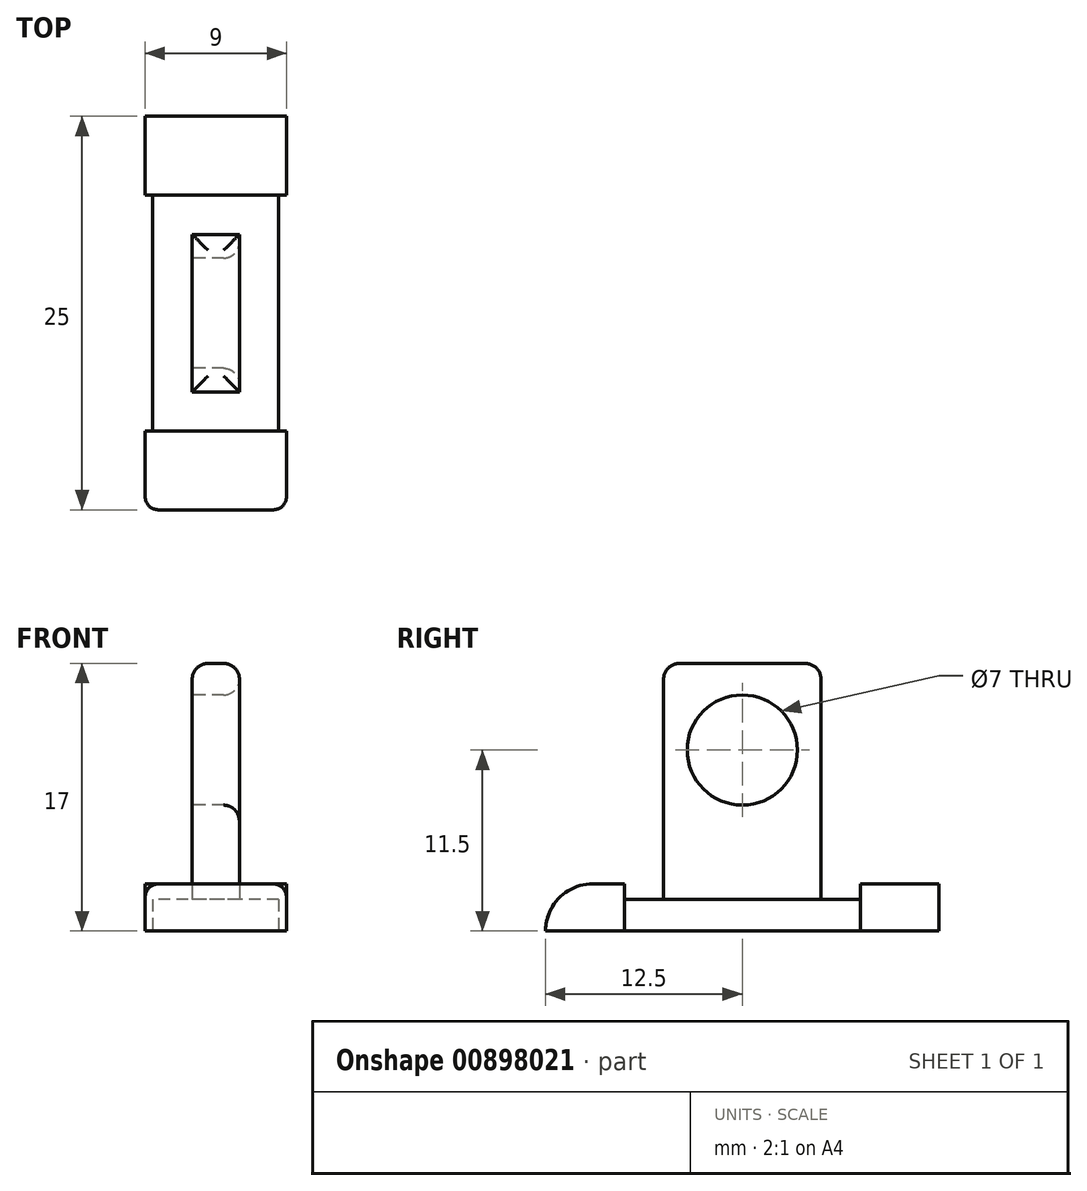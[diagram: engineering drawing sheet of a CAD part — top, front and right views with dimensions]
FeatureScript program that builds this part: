
annotation { "Feature Type Name" : "Feature", "Feature Type Description" : "" }
export const myFeature = defineFeature(function(context is Context, id is Id, definition is map)
    precondition{}
    {
        {
            var Q0;
            Q0=qCreatedBy(makeId("Top.planeOp"),FACE);
            var sketch = newSketch(context, id + "F0", { "sketchPlane" : qUnion([Q0])});
            skLineSegment(sketch, "E0.bottom", {"start": v(4, -10) * mm, "end": v(-4, -10) * mm});
            skLineSegment(sketch, "E0.top", {"start": v(4, 10) * mm, "end": v(-4, 10) * mm});
            skLineSegment(sketch, "E0.left", {"start": v(4, -10) * mm, "end": v(4, 10) * mm});
            skLineSegment(sketch, "E0.right", {"start": v(-4, -10) * mm, "end": v(-4, 10) * mm});
            skPoint(sketch, "E0.middle", {"position": v(0, 0) * mm});
            skLineSegment(sketch, "E1.bottom", {"start": v(4.5, 7.5) * mm, "end": v(-4.5, 7.5) * mm});
            skLineSegment(sketch, "E1.top", {"start": v(4.5, 12.5) * mm, "end": v(-4.5, 12.5) * mm});
            skLineSegment(sketch, "E1.left", {"start": v(4.5, 7.5) * mm, "end": v(4.5, 12.5) * mm});
            skLineSegment(sketch, "E1.right", {"start": v(-4.5, 7.5) * mm, "end": v(-4.5, 12.5) * mm});
            skPoint(sketch, "E1.middle", {"position": v(0, 10) * mm});
            skLineSegment(sketch, "E2.bottom", {"start": v(4.5, -12.5) * mm, "end": v(-4.5, -12.5) * mm});
            skLineSegment(sketch, "E2.top", {"start": v(4.5, -7.5) * mm, "end": v(-4.5, -7.5) * mm});
            skLineSegment(sketch, "E2.left", {"start": v(4.5, -12.5) * mm, "end": v(4.5, -7.5) * mm});
            skLineSegment(sketch, "E2.right", {"start": v(-4.5, -12.5) * mm, "end": v(-4.5, -7.5) * mm});
            skPoint(sketch, "E2.middle", {"position": v(0, -10) * mm});
            skSolve(sketch);
        }
        {
            var Q0;
            {var subQ0=sQuery(id+"F0.wireOp",EDGE,"E2.top");var subQ1=sQuery(id+"F0.wireOp",EDGE,"E0.left");var subQ2=makeQuery(id+"F0.imprint","INTERSECT",VERTEX,{"derivedFrom":[subQ1,subQ0]});Q0=makeQuery(id+"F0.imprint","IMPRINT",FACE,{"disambiguationData":[TD([[makeQuery(id+"F0.imprint","IMPRINT",EDGE,{"disambiguationData":[TD([[subQ2,-1.0]])],"derivedFrom":subQ1}),1.0]])]});}
            extrude(context, id + "F1", {"entities" : qUnion([Q0]), "depth" : 2 * mm, "offsetDistance" : 25 * mm});
        }
        {
            var Q0;
            {var subQ0=sQuery(id+"F0.wireOp",EDGE,"E0.bottom");Q0=makeQuery(id+"F0.imprint","IMPRINT",FACE,{"disambiguationData":[TD([[makeQuery(id+"F0.imprint","IMPRINT",EDGE,{"derivedFrom":subQ0}),-1.0]])]});}
            var Q1;
            {var subQ1=sQuery(id+"F0.wireOp",EDGE,"E0.bottom");Q1=makeQuery(id+"F0.imprint","IMPRINT",FACE,{"disambiguationData":[TD([[makeQuery(id+"F0.imprint","IMPRINT",EDGE,{"derivedFrom":subQ1}),1.0]])]});}
            var Q2;
            {var subQ5=sQuery(id+"F0.wireOp",EDGE,"E0.top");Q2=makeQuery(id+"F0.imprint","IMPRINT",FACE,{"disambiguationData":[TD([[makeQuery(id+"F0.imprint","IMPRINT",EDGE,{"derivedFrom":subQ5}),-1.0]])]});}
            var Q3;
            {var subQ0=sQuery(id+"F0.wireOp",EDGE,"E0.top");Q3=makeQuery(id+"F0.imprint","IMPRINT",FACE,{"disambiguationData":[TD([[makeQuery(id+"F0.imprint","IMPRINT",EDGE,{"derivedFrom":subQ0}),1.0]])]});}
            extrude(context, id + "F2", {"entities" : qUnion([Q0, Q1, Q2, Q3]), "operationType" : NewBodyOperationType.ADD, "depth" : 3 * mm, "offsetDistance" : 25 * mm});
        }
        {
            var Q0;
            Q0=makeQuery(id+"F2.opExtrude","CAP_EDGE",EDGE,{"disambiguationData":[OSD([sQuery(id+"F0.wireOp",EDGE,"E2.bottom")])],"isStart":false});
            fillet(context, id + "F3", {"entities" : qUnion([Q0]), "radius" : 3 * mm, "tangentPropagation" : true, "allowEdgeOverflow" : false});
        }
        {
            var Q0;
            Q0=makeQuery(id+"F3.opFillet","BLEND_EDGE",EDGE,{"blendedFrom":[makeQuery(id+"F2.opExtrude","CAP_EDGE",EDGE,{"disambiguationData":[OSD([sQuery(id+"F0.wireOp",EDGE,"E2.bottom")])],"isStart":false}),makeQuery(id+"F2.opExtrude","SWEPT_FACE",FACE,{"disambiguationData":[OSD([sQuery(id+"F0.wireOp",EDGE,"E2.left")])]})],"blendedInto":[makeQuery(id+"F2.opExtrude","SWEPT_FACE",FACE,{"disambiguationData":[OSD([sQuery(id+"F0.wireOp",EDGE,"E2.left")])]})]});
            var Q1;
            Q1=makeQuery(id+"F3.opFillet","BLEND_EDGE",EDGE,{"blendedFrom":[makeQuery(id+"F2.opExtrude","CAP_EDGE",EDGE,{"disambiguationData":[OSD([sQuery(id+"F0.wireOp",EDGE,"E2.bottom")])],"isStart":false}),makeQuery(id+"F2.opExtrude","SWEPT_FACE",FACE,{"disambiguationData":[OSD([sQuery(id+"F0.wireOp",EDGE,"E2.right")])]})],"blendedInto":[makeQuery(id+"F2.opExtrude","SWEPT_FACE",FACE,{"disambiguationData":[OSD([sQuery(id+"F0.wireOp",EDGE,"E2.right")])]})]});
            fillet(context, id + "F4", {"entities" : qUnion([Q0, Q1]), "radius" : 1 * mm, "tangentPropagation" : true, "rho" : 0.5, "crossSection" : FilletCrossSection.CONIC, "allowEdgeOverflow" : false});
        }
        {
            var Q0;
            Q0=makeQuery(id+"F1.opExtrude","CAP_FACE",FACE,{"disambiguationData":[OSD([sQuery(id+"F0.wireOp",EDGE,"E0.left"),sQuery(id+"F0.wireOp",EDGE,"E0.right"),sQuery(id+"F0.wireOp",EDGE,"E1.bottom"),sQuery(id+"F0.wireOp",EDGE,"E2.top")])],"isStart":false});
            var sketch = newSketch(context, id + "F5", { "sketchPlane" : qUnion([Q0])});
            skLineSegment(sketch, "E3.bottom", {"start": v(1.5, -5) * mm, "end": v(-1.5, -5) * mm});
            skLineSegment(sketch, "E3.top", {"start": v(1.5, 5) * mm, "end": v(-1.5, 5) * mm});
            skLineSegment(sketch, "E3.left", {"start": v(1.5, -5) * mm, "end": v(1.5, 5) * mm});
            skLineSegment(sketch, "E3.right", {"start": v(-1.5, -5) * mm, "end": v(-1.5, 5) * mm});
            skPoint(sketch, "E3.middle", {"position": v(0, 0) * mm});
            skSolve(sketch);
        }
        {
            var Q0;
            Q0=makeQuery(id+"F5.imprint","IMPRINT",FACE,{"disambiguationData":[TD([[makeQuery(id+"F5.imprint","IMPRINT",EDGE,{"derivedFrom":sQuery(id+"F5.wireOp",EDGE,"E3.bottom")}),-1.0]])]});
            extrude(context, id + "F6", {"entities" : qUnion([Q0]), "operationType" : NewBodyOperationType.ADD, "depth" : 15 * mm, "offsetDistance" : 25 * mm});
        }
        {
            var Q0;
            Q0=makeQuery(id+"F6.opExtrude","SWEPT_FACE",FACE,{"disambiguationData":[OSD([sQuery(id+"F5.wireOp",EDGE,"E3.right")])]});
            var sketch = newSketch(context, id + "F7", { "sketchPlane" : qUnion([Q0])});
            skSolve(sketch);
        }
        {
            var Q0;
            {var subQ0=sQuery(id+"F5.wireOp",EDGE,"E3.right");Q0=makeQuery(id+"F7.imprint","IMPRINT",FACE,{"disambiguationData":[TD([[makeQuery(id+"F7.imprint","IMPRINT",EDGE,{"derivedFrom":makeQuery(id+"F6.opExtrude","CAP_EDGE",EDGE,{"disambiguationData":[OSD([subQ0])],"isStart":false})}),1.0]])]});}
            var sketch = newSketch(context, id + "F8", { "sketchPlane" : qUnion([Q0])});
            skCircle(sketch, "E4", {"center": v(0, 11.5) * mm, "radius": 3.5 * mm});
            skSolve(sketch);
        }
        {
            var Q0;
            Q0=makeQuery(id+"F8.imprint","IMPRINT",FACE,{"disambiguationData":[TD([[makeQuery(id+"F8.imprint","IMPRINT",EDGE,{"derivedFrom":sQuery(id+"F8.wireOp",EDGE,"E4")}),1.0]])]});
            extrude(context, id + "F9", {"entities" : qUnion([Q0]), "operationType" : NewBodyOperationType.REMOVE, "endBound" : BoundingType.THROUGH_ALL, "oppositeDirection" : true, "depth" : 25 * mm, "offsetDistance" : 25 * mm});
        }
        {
            var Q0;
            Q0=makeQuery(id+"F6.opExtrude","CAP_EDGE",EDGE,{"disambiguationData":[OSD([sQuery(id+"F5.wireOp",EDGE,"E3.left")])],"isStart":false});
            var Q1;
            Q1=makeQuery(id+"F6.opExtrude","CAP_EDGE",EDGE,{"disambiguationData":[OSD([sQuery(id+"F5.wireOp",EDGE,"E3.bottom")])],"isStart":false});
            var Q2;
            Q2=makeQuery(id+"F6.opExtrude","CAP_EDGE",EDGE,{"disambiguationData":[OSD([sQuery(id+"F5.wireOp",EDGE,"E3.right")])],"isStart":false});
            var Q3;
            Q3=makeQuery(id+"F6.opExtrude","CAP_EDGE",EDGE,{"disambiguationData":[OSD([sQuery(id+"F5.wireOp",EDGE,"E3.top")])],"isStart":false});
            var Q4;
            Q4=makeQuery(id+"F9.boolean.opBoolean","INTERSECT",EDGE,{"derivedFrom":[makeQuery(id+"F6.opExtrude","SWEPT_FACE",FACE,{"disambiguationData":[OSD([sQuery(id+"F5.wireOp",EDGE,"E3.left")])]}),makeQuery(id+"F9.opExtrude","SWEPT_FACE",FACE,{"disambiguationData":[OSD([sQuery(id+"F8.wireOp",EDGE,"E4")])]})]});
            var Q5;
            Q5=makeQuery(id+"F9.boolean.opBoolean","COPY",EDGE,{"derivedFrom":makeQuery(id+"F9.opExtrude","CAP_EDGE",EDGE,{"disambiguationData":[OSD([sQuery(id+"F8.wireOp",EDGE,"E4")])],"isStart":true})});
            fillet(context, id + "F10", {"entities" : qUnion([Q0, Q1, Q2, Q3, Q4, Q5]), "radius" : 1 * mm, "tangentPropagation" : true, "allowEdgeOverflow" : false});
        }
    });
